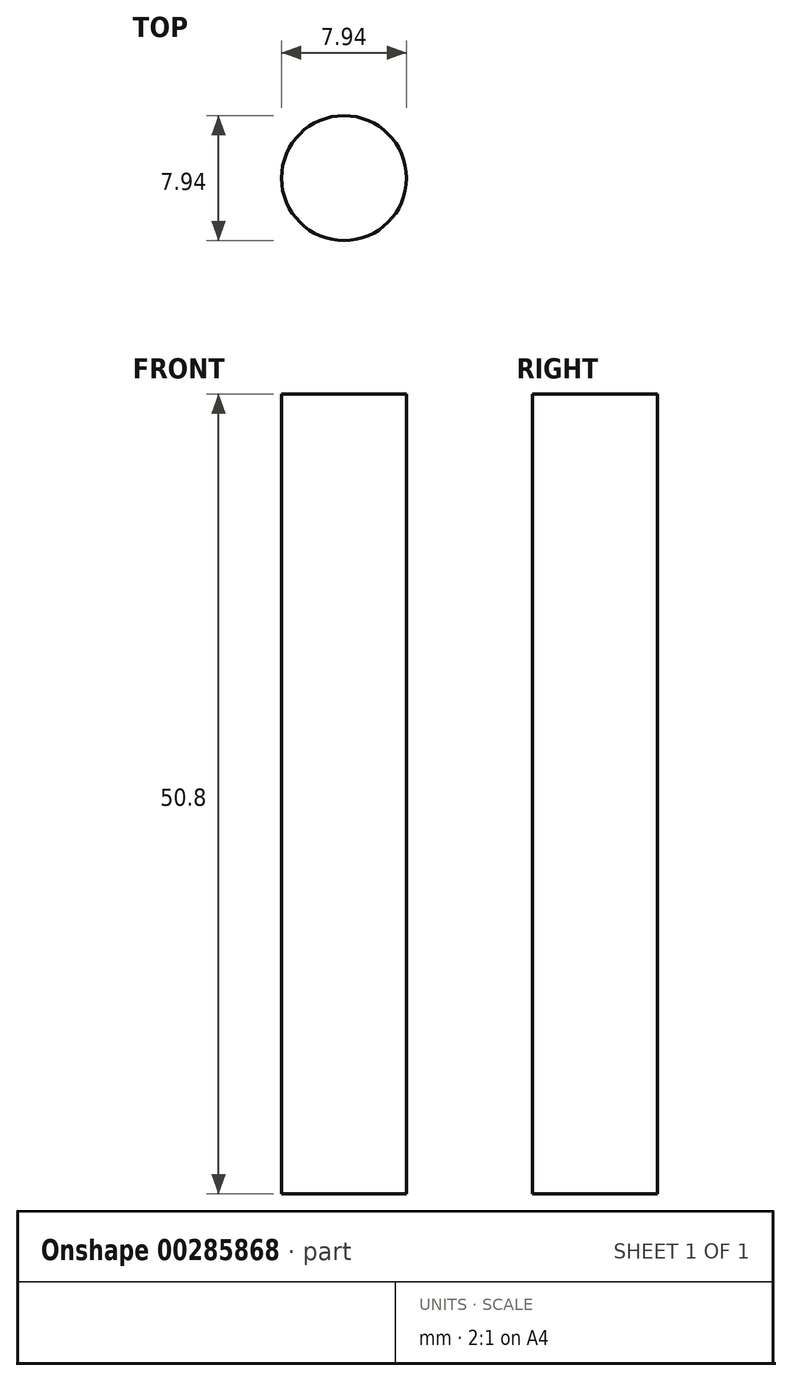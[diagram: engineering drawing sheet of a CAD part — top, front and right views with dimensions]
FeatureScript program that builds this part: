
annotation { "Feature Type Name" : "Feature", "Feature Type Description" : "" }
export const myFeature = defineFeature(function(context is Context, id is Id, definition is map)
    precondition{}
    {
        {
            var Q0;
            Q0=qCreatedBy(makeId("Top.planeOp"),FACE);
            var sketch = newSketch(context, id + "F0", { "sketchPlane" : qUnion([Q0])});
            skCircle(sketch, "E0", {"center": v(0, 0) * mm, "radius": 3.97 * mm});
            skSolve(sketch);
        }
        {
            var Q0;
            Q0=makeQuery(id+"F0.imprint","IMPRINT",FACE,{"disambiguationData":[TD([[makeQuery(id+"F0.imprint","IMPRINT",EDGE,{"derivedFrom":sQuery(id+"F0.wireOp",EDGE,"E0")}),1.0]])]});
            extrude(context, id + "F1", {"entities" : qUnion([Q0]), "depth" : 50.8 * mm});
        }
    });
